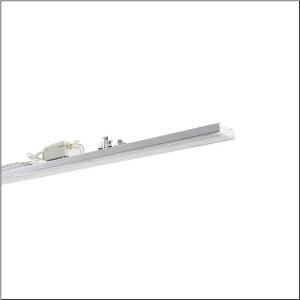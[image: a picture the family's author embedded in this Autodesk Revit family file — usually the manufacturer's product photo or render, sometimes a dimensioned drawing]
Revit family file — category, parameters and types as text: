
# Revit family: licross_r__21_recessed_mo_52te10dn4axg_60c1
name_source: partatom
category: Lighting Fixtures
units: mm (PartAtom-declared; Revit-internal decimal feet)

## family parameters
Cut with Voids When Loaded = No
Host = Face
Light Source = No
Part Type = Normal
Room Calculation Point = No
Round Connector Dimension = Use Diameter
Shared = No

## types (1)
- --- (1 x LED, 10000 lm, 58 W, 4000K)
    Apparent Load = 58 VA
    CIE Flux Codes = 50 81 96 100 100
    Color Rendering = 80
    Color Temperature = 4000K
    Default Elevation = 1800 mm
    Description = Licross® 21 Recessed MO, luminaire insert, of sheet steel, galvanised, coil coated, white, length: 1.500mm, width: 66mm, height: 67mm, LED rated luminous flux: 10.000lm, light colour: 840, control gear: DALI 2, with plug, 5-pole, with phase selection, mains connection: 220..240V, AC, 50/60Hz, rated input power: 58W, halogen-free wiring, primary optical cover: cover, of PMMA, light emission: direct distribution, primary light characteristic: symmetric, protection rating (complete): IP54, insulation class (complete): insulation class I (protective earthing), certification: CE, ENEC, VDE, UKCA, protection symbol: D if used in an environment with non-conductive dust loads with corresponding accessories, impact resistance: IK06, permissible ambient temperature for indoor applications: -25..+35°C, corresponds to IFS (International Featured Standards) requirements for safety and quality in the food industry, reducing of maximum allowable ambient temperature of 5°C with ceiling mounting, LABS conformity tested according to VDMA 24364:2018-05, packaging unit: 1 piece
    Height = 58 mm
    Lamp = 1 x LED
    Lamp Light Flux = 10000 lm
    Lamp Power = 58 W
    Lamp count = 1
    Length = 1500 mm
    Luminous efficacy = 172 lm/W
    Manufacturer = Siteco
    ModVariant = No
    Model = 52TE10DN4AXG
    Mounting Place = Ceiling
    Mounting Type = Pendant
    Number of Poles = 1
    OnlyDefault = Yes
    Power Factor = 1
    Product Name = Licross® 21 Recessed MO
    Product group = luminaire insert
    ProductGroupID = 901
    Protection Class = Protection class I
    Protection Degree = IP 54
    RLX_Detail_Level = 1
    RLX_Emergency_Light_Flux = 0 lm
    RLX_Emergency_Type = 0
    RLX_Emergency_Type_DB = No
    RlxData = <blob elided: 24333 chars, md5=0b751496>
    Socket = socket
    Standby Power = 0 W
    System Light Flux = 10000 lm
    System Power = 58 W
    Type Comments = factory setting: luminous flux: 100 % | dim-lin: 254 | 390 mA
    Type Image = l_1296930.jpg
    URL = http://relux.com
    VarID = @adj_059119
    Voltage = 0 V
    Weight = 0.00 kg
    Width = 66 mm

## geometry (parser evidence)
native form markers: Blend x4, Sweep x10
no freeform markers — native parametric forms only
